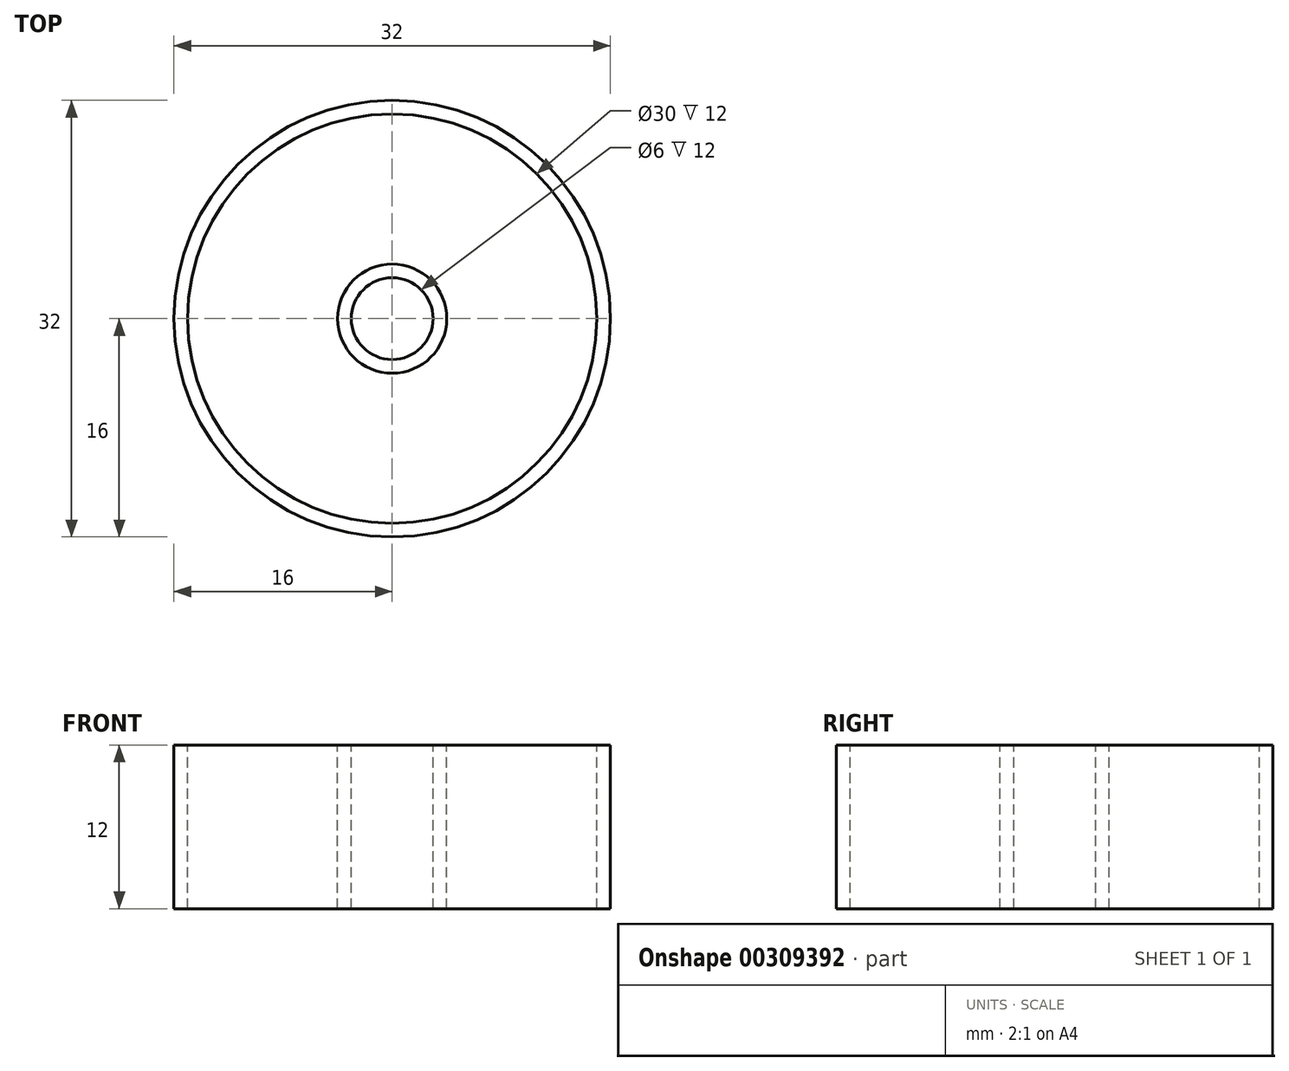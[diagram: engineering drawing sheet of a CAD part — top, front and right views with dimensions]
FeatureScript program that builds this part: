
annotation { "Feature Type Name" : "Feature", "Feature Type Description" : "" }
export const myFeature = defineFeature(function(context is Context, id is Id, definition is map)
    precondition{}
    {
        {
            var Q0;
            Q0=qCreatedBy(makeId("Top.planeOp"),FACE);
            var sketch = newSketch(context, id + "F0", { "sketchPlane" : qUnion([Q0])});
            skCircle(sketch, "E0", {"center": v(0, 0) * mm, "radius": 15 * mm});
            skCircle(sketch, "E1", {"center": v(0, 0) * mm, "radius": 3 * mm});
            skCircle(sketch, "E2", {"center": v(0, 0) * mm, "radius": 4 * mm});
            skCircle(sketch, "E3", {"center": v(0, 0) * mm, "radius": 16 * mm});
            skFitSpline(sketch, "E4", {"points": [v(0, 15) * mm, v(5, 8.66) * mm, v(4, 0) * mm], "startDerivative": vector(13.18, -11.93) * mm, "endDerivative": vector(-5.06, -18.03) * mm});
            skFitSpline(sketch, "E5", {"points": [v(7.5, 13) * mm, v(8.66, 5) * mm, v(3.46, -2) * mm], "startDerivative": vector(5.45, -16.92) * mm, "endDerivative": vector(-13.4, -13.09) * mm});
            skFitSpline(sketch, "E6", {"points": [v(13, 7.5) * mm, v(10, 0) * mm, v(2, -3.46) * mm], "startDerivative": vector(-3.74, -17.38) * mm, "endDerivative": vector(-18.15, -4.63) * mm});
            skFitSpline(sketch, "E7", {"points": [v(15, 0) * mm, v(8.66, -5) * mm, v(0, -4) * mm], "startDerivative": vector(-11.93, -13.18) * mm, "endDerivative": vector(-18.03, 5.06) * mm});
            skFitSpline(sketch, "E8", {"points": [v(13, -7.5) * mm, v(5, -8.66) * mm, v(-2, -3.46) * mm], "startDerivative": vector(-16.92, -5.45) * mm, "endDerivative": vector(-13.09, 13.4) * mm});
            skFitSpline(sketch, "E9", {"points": [v(7.5, -13) * mm, v(0, -10) * mm, v(-3.46, -2) * mm], "startDerivative": vector(-17.38, 3.74) * mm, "endDerivative": vector(-4.63, 18.15) * mm});
            skFitSpline(sketch, "E10", {"points": [v(0, -15) * mm, v(-5, -8.66) * mm, v(-4, 0) * mm], "startDerivative": vector(-13.18, 11.93) * mm, "endDerivative": vector(5.06, 18.03) * mm});
            skFitSpline(sketch, "E11", {"points": [v(-7.5, -13) * mm, v(-8.66, -5) * mm, v(-3.46, 2) * mm], "startDerivative": vector(-5.45, 16.92) * mm, "endDerivative": vector(13.4, 13.09) * mm});
            skFitSpline(sketch, "E12", {"points": [v(-15, 0) * mm, v(-8.66, 5) * mm, v(0, 4) * mm], "startDerivative": vector(11.93, 13.16) * mm, "endDerivative": vector(18.03, -5.04) * mm});
            skFitSpline(sketch, "E13", {"points": [v(-13, -7.5) * mm, v(-10, 0) * mm, v(-2, 3.46) * mm], "startDerivative": vector(3.74, 17.38) * mm, "endDerivative": vector(18.15, 4.63) * mm});
            skFitSpline(sketch, "E14", {"points": [v(-12.97, 7.57) * mm, v(-5, 8.66) * mm, v(2, 3.46) * mm], "startDerivative": vector(16.89, 5.27) * mm, "endDerivative": vector(13.08, -13.35) * mm});
            skFitSpline(sketch, "E15", {"points": [v(-7.5, 13) * mm, v(0.06, 10) * mm, v(3.46, 2) * mm], "startDerivative": vector(17.5, -3.72) * mm, "endDerivative": vector(4.5, -18.18) * mm});
            skSolve(sketch);
        }
        {
            var Q0;
            Q0=makeQuery(id+"F0.imprint","IMPRINT",FACE,{"disambiguationData":[TD([[makeQuery(id+"F0.imprint","IMPRINT",EDGE,{"derivedFrom":sQuery(id+"F0.wireOp",EDGE,"E1")}),-1.0]])]});
            var Q1;
            Q1=makeQuery(id+"F0.imprint","IMPRINT",FACE,{"disambiguationData":[TD([[makeQuery(id+"F0.imprint","IMPRINT",EDGE,{"derivedFrom":sQuery(id+"F0.wireOp",EDGE,"E3")}),1.0]])]});
            extrude(context, id + "F1", {"entities" : qUnion([Q0, Q1]), "oppositeDirection" : true, "depth" : 12 * mm});
        }
    });
